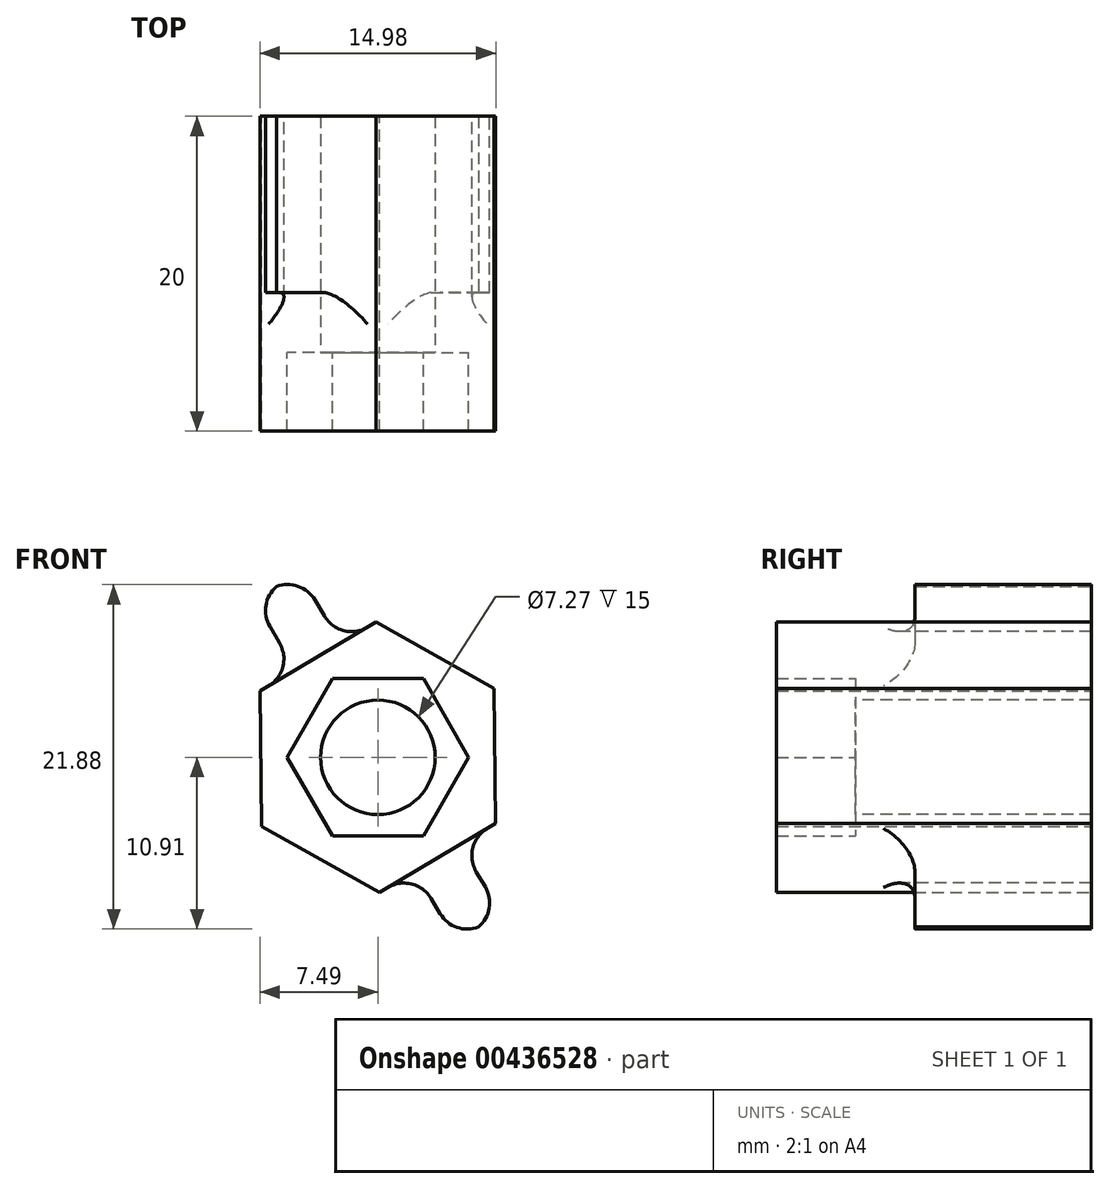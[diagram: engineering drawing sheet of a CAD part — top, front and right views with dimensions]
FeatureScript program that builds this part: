
annotation { "Feature Type Name" : "Feature", "Feature Type Description" : "" }
export const myFeature = defineFeature(function(context is Context, id is Id, definition is map)
    precondition{}
    {
        {
            var Q0;
            Q0=qCreatedBy(makeId("Front.planeOp"),FACE);
            var sketch = newSketch(context, id + "F0", { "sketchPlane" : qUnion([Q0])});
            skCircle(sketch, "E0.cCircle", {"center": v(0, 0) * mm, "radius": 5 * mm, "construction": true});
            skLineSegment(sketch, "E0.0", {"start": v(2.89, 5) * mm, "end": v(5.77, 0) * mm});
            skLineSegment(sketch, "E0.1", {"start": v(5.77, 0) * mm, "end": v(2.89, -5) * mm});
            skLineSegment(sketch, "E0.2", {"start": v(2.89, -5) * mm, "end": v(-2.89, -5) * mm});
            skLineSegment(sketch, "E0.3", {"start": v(-2.89, -5) * mm, "end": v(-5.77, 0) * mm});
            skLineSegment(sketch, "E0.4", {"start": v(-5.77, 0) * mm, "end": v(-2.89, 5) * mm});
            skLineSegment(sketch, "E0.5", {"start": v(-2.89, 5) * mm, "end": v(2.89, 5) * mm});
            skPoint(sketch, "E0.0.midPoint", {"position": v(4.33, 2.5) * mm});
            skCircle(sketch, "E1.cCircle", {"center": v(0, 0) * mm, "radius": 7.44 * mm, "construction": true});
            skLineSegment(sketch, "E1.0", {"start": v(-0.1, 8.59) * mm, "end": v(7.38, 4.38) * mm});
            skLineSegment(sketch, "E1.1", {"start": v(7.38, 4.38) * mm, "end": v(7.49, -4.2) * mm});
            skLineSegment(sketch, "E1.2", {"start": v(7.49, -4.2) * mm, "end": v(0.1, -8.59) * mm});
            skLineSegment(sketch, "E1.3", {"start": v(0.1, -8.59) * mm, "end": v(-7.38, -4.38) * mm});
            skLineSegment(sketch, "E1.4", {"start": v(-7.38, -4.38) * mm, "end": v(-7.49, 4.2) * mm});
            skLineSegment(sketch, "E1.5", {"start": v(-7.49, 4.2) * mm, "end": v(-0.1, 8.59) * mm});
            skPoint(sketch, "E1.0.midPoint", {"position": v(3.64, 6.48) * mm});
            skSolve(sketch);
        }
        {
            var Q0;
            Q0=makeQuery(id+"F0.imprint","IMPRINT",FACE,{"disambiguationData":[TD([[makeQuery(id+"F0.imprint","IMPRINT",EDGE,{"derivedFrom":sQuery(id+"F0.wireOp",EDGE,"E0.0")}),1.0]])]});
            extrude(context, id + "F1", {"entities" : qUnion([Q0]), "depth" : 20 * mm});
        }
        {
            var Q0;
            Q0=makeQuery(id+"F0.imprint","IMPRINT",FACE,{"disambiguationData":[TD([[makeQuery(id+"F0.imprint","IMPRINT",EDGE,{"derivedFrom":sQuery(id+"F0.wireOp",EDGE,"E0.0")}),-1.0]])]});
            extrude(context, id + "F2", {"entities" : qUnion([Q0]), "operationType" : NewBodyOperationType.ADD, "depth" : 15 * mm});
        }
        {
            var Q0;
            Q0=makeQuery(id+"F2.opExtrude","CAP_FACE",FACE,{"disambiguationData":[OSD([sQuery(id+"F0.wireOp",EDGE,"E0.0"),sQuery(id+"F0.wireOp",EDGE,"E0.1"),sQuery(id+"F0.wireOp",EDGE,"E0.2"),sQuery(id+"F0.wireOp",EDGE,"E0.3"),sQuery(id+"F0.wireOp",EDGE,"E0.4"),sQuery(id+"F0.wireOp",EDGE,"E0.5")])],"isStart":false});
            var sketch = newSketch(context, id + "F3", { "sketchPlane" : qUnion([Q0])});
            skCircle(sketch, "E2", {"center": v(0, 0) * mm, "radius": 3.64 * mm});
            skSolve(sketch);
        }
        {
            var Q0;
            Q0=makeQuery(id+"F1.opExtrude","SWEPT_FACE",FACE,{"disambiguationData":[OSD([sQuery(id+"F0.wireOp",EDGE,"E1.5")])]});
            var sketch = newSketch(context, id + "F4", { "sketchPlane" : qUnion([Q0])});
            skLineSegment(sketch, "E3.bottom", {"start": v(-1.66, 0) * mm, "end": v(1.66, 0) * mm});
            skLineSegment(sketch, "E3.top", {"start": v(-1.66, -11.2) * mm, "end": v(1.66, -11.2) * mm});
            skLineSegment(sketch, "E3.left", {"start": v(-1.66, 0) * mm, "end": v(-1.66, -11.2) * mm});
            skLineSegment(sketch, "E3.right", {"start": v(1.66, 0) * mm, "end": v(1.66, -11.2) * mm});
            skPoint(sketch, "E3.middle", {"position": v(0, -5.6) * mm});
            skSolve(sketch);
        }
        {
            var Q0;
            Q0=makeQuery(id+"F4.imprint","IMPRINT",FACE,{"disambiguationData":[TD([[makeQuery(id+"F4.imprint","IMPRINT",EDGE,{"derivedFrom":sQuery(id+"F4.wireOp",EDGE,"E3.bottom")}),-1.0]])]});
            extrude(context, id + "F5", {"entities" : qUnion([Q0]), "operationType" : NewBodyOperationType.ADD, "depth" : 5.2 * mm, "hasSecondDirection" : true, "secondDirectionOppositeDirection" : true, "secondDirectionDepth" : 20 * mm});
        }
        {
            var Q0;
            Q0 = qSketchRegion(id + "F3", true);
            extrude(context, id + "F6", {"entities" : qUnion([Q0]), "operationType" : NewBodyOperationType.REMOVE, "oppositeDirection" : true, "depth" : 25 * mm});
        }
        {
            var Q0;
            Q0=makeQuery(id+"F5.boolean.opBoolean","INTERSECT",EDGE,{"derivedFrom":[makeQuery(id+"F1.opExtrude","SWEPT_FACE",FACE,{"disambiguationData":[OSD([sQuery(id+"F0.wireOp",EDGE,"E1.5")])]}),makeQuery(id+"F5.opExtrude","SWEPT_FACE",FACE,{"disambiguationData":[OSD([sQuery(id+"F4.wireOp",EDGE,"E3.left")])]})]});
            var Q1;
            Q1=makeQuery(id+"F5.opExtrude","CAP_EDGE",EDGE,{"disambiguationData":[OSD([sQuery(id+"F4.wireOp",EDGE,"E3.left")])],"isStart":false});
            var Q2;
            Q2=makeQuery(id+"F5.opExtrude","CAP_EDGE",EDGE,{"disambiguationData":[OSD([sQuery(id+"F4.wireOp",EDGE,"E3.right")])],"isStart":false});
            var Q3;
            Q3=makeQuery(id+"F5.boolean.opBoolean","INTERSECT",EDGE,{"derivedFrom":[makeQuery(id+"F1.opExtrude","SWEPT_FACE",FACE,{"disambiguationData":[OSD([sQuery(id+"F0.wireOp",EDGE,"E1.5")])]}),makeQuery(id+"F5.opExtrude","SWEPT_FACE",FACE,{"disambiguationData":[OSD([sQuery(id+"F4.wireOp",EDGE,"E3.right")])]})]});
            var Q4;
            Q4=makeQuery(id+"F5.boolean.opBoolean","INTERSECT",EDGE,{"derivedFrom":[makeQuery(id+"F1.opExtrude","SWEPT_FACE",FACE,{"disambiguationData":[OSD([sQuery(id+"F0.wireOp",EDGE,"E1.2")])]}),makeQuery(id+"F5.opExtrude","SWEPT_FACE",FACE,{"disambiguationData":[OSD([sQuery(id+"F4.wireOp",EDGE,"E3.right")])]})]});
            var Q5;
            Q5=makeQuery(id+"F5.boolean.opBoolean","INTERSECT",EDGE,{"derivedFrom":[makeQuery(id+"F1.opExtrude","SWEPT_FACE",FACE,{"disambiguationData":[OSD([sQuery(id+"F0.wireOp",EDGE,"E1.2")])]}),makeQuery(id+"F5.opExtrude","SWEPT_FACE",FACE,{"disambiguationData":[OSD([sQuery(id+"F4.wireOp",EDGE,"E3.left")])]})]});
            var Q6;
            Q6=makeQuery(id+"F5.opExtrude","CAP_EDGE",EDGE,{"disambiguationData":[OSD([sQuery(id+"F4.wireOp",EDGE,"E3.left")])],"isStart":true});
            var Q7;
            Q7=makeQuery(id+"F5.opExtrude","CAP_EDGE",EDGE,{"disambiguationData":[OSD([sQuery(id+"F4.wireOp",EDGE,"E3.right")])],"isStart":true});
            var Q8;
            Q8=makeQuery(id+"F5.boolean.opBoolean","INTERSECT",EDGE,{"derivedFrom":[makeQuery(id+"F1.opExtrude","SWEPT_FACE",FACE,{"disambiguationData":[OSD([sQuery(id+"F0.wireOp",EDGE,"E1.5")])]}),makeQuery(id+"F5.opExtrude","SWEPT_FACE",FACE,{"disambiguationData":[OSD([sQuery(id+"F4.wireOp",EDGE,"E3.top")])]})]});
            var Q9;
            Q9=makeQuery(id+"F5.boolean.opBoolean","INTERSECT",EDGE,{"derivedFrom":[makeQuery(id+"F1.opExtrude","SWEPT_FACE",FACE,{"disambiguationData":[OSD([sQuery(id+"F0.wireOp",EDGE,"E1.2")])]}),makeQuery(id+"F5.opExtrude","SWEPT_FACE",FACE,{"disambiguationData":[OSD([sQuery(id+"F4.wireOp",EDGE,"E3.top")])]})]});
            fillet(context, id + "F7", {"entities" : qUnion([Q0, Q1, Q2, Q3, Q4, Q5, Q6, Q7, Q8, Q9]), "radius" : 2 * mm, "tangentPropagation" : true, "allowEdgeOverflow" : false});
        }
    });
